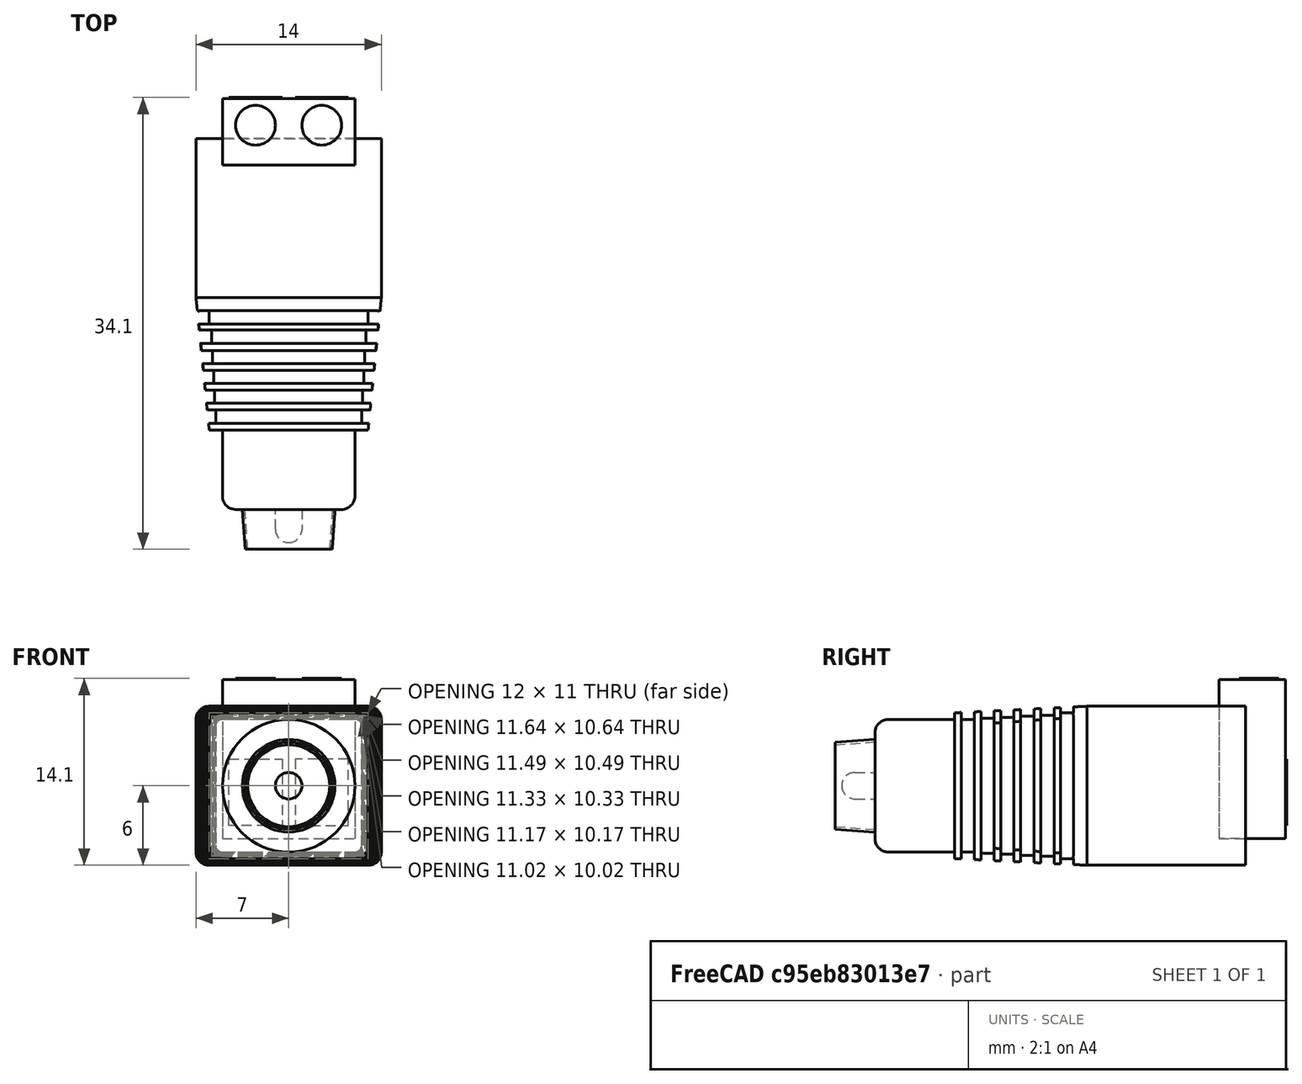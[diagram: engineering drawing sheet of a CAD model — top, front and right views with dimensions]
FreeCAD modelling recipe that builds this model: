
FCSTD DOCUMENT  (FreeCAD 1.1R20260414 (Git shallow))
Label: dc_to_2wire
License: All rights reserved
LicenseURL: https://en.wikipedia.org/wiki/All_rights_reserved
objects: Sketcher::SketchObject×9, PartDesign::Pad×7, App::Point×5, PartDesign::Plane×5, PartDesign::Body×4, App::Link×4, App::FeaturePython×4, PartDesign::Fillet×2, PartDesign::Mirrored×2, PartDesign::AdditiveLoft×1, PartDesign::SubtractivePipe×1, Assembly::JointGroup×1, Assembly::AssemblyObject×1
note: 64 computed .brp shape members not serialized (recipe doc carries the construction recipe); baked Part::Feature solids carry a one-line shape summary decoded from their .brp

FEATURE [App::Point] Origin001
  Role = Origin
FEATURE [Sketcher::SketchObject] Sketch
  ArcFitTolerance = 1e-06
  AttachmentSupport = -> [Origin]
  ExternalTypes = [0]
  FullyConstrained = true
  MakeInternals = false
  MapMode = 5
  Placement = pos=(0,0,0) rot=(1,0,0;1.5708rad)
  _ExternalGeoVersion = 1
  sketch-geometry (10):
    g0: LineSegment StartX=-6 StartY=-6 StartZ=0 EndX=6 EndY=-6 EndZ=0
    g1: LineSegment StartX=7 StartY=-5 StartZ=0 EndX=7 EndY=5 EndZ=0
    g2: LineSegment StartX=6 StartY=6 StartZ=0 EndX=-6 EndY=6 EndZ=0
    g3: LineSegment StartX=-7 StartY=5 StartZ=0 EndX=-7 EndY=-5 EndZ=0
    g4: ArcOfCircle CenterX=-6 CenterY=-5 CenterZ=0 NormalX=0 NormalY=0 NormalZ=1 AngleXU=0 Radius=1 StartAngle=3.14159 EndAngle=4.71239
    g5: ArcOfCircle CenterX=6 CenterY=-5 CenterZ=0 NormalX=0 NormalY=0 NormalZ=1 AngleXU=0 Radius=1 StartAngle=4.71239 EndAngle=6.28319
    g6: ArcOfCircle CenterX=6 CenterY=5 CenterZ=0 NormalX=0 NormalY=0 NormalZ=1 AngleXU=0 Radius=1 StartAngle=0 EndAngle=1.5708
    g7: ArcOfCircle CenterX=-6 CenterY=5 CenterZ=0 NormalX=0 NormalY=0 NormalZ=1 AngleXU=0 Radius=1 StartAngle=1.5708 EndAngle=3.14159
    g8: GeomPoint [constr] X=7 Y=6 Z=0
    g9: GeomPoint [constr] X=-2.33e-14 Y=2.6e-14 Z=0
  constraints (22):
    c: Tangent(g0,g4) = -1.5708
    c: Tangent(g0,g5) = -1.5708
    c: Tangent(g1,g5) = -1.5708
    c: Tangent(g1,g6) = -1.5708
    c: Tangent(g2,g6) = -1.5708
    c: Tangent(g2,g7) = -1.5708
    c: Tangent(g3,g7) = -1.5708
    c: Tangent(g3,g4) = -1.5708
    c: Horizontal(g0)
    c: Horizontal(g2)
    c: Vertical(g1)
    c: Vertical(g3)
    c: Equal(g4,g5)
    c: Equal(g5,g6)
    c: Equal(g6,g7)
    c: Symmetric(g2,g0,g9)
    c: PointOnObject(g8,g1)
    c: PointOnObject(g8,g2)
    c: Distance(g1,g3) = 14
    c: Distance(g0,g2) = 12
    c: Radius(g5) = 1
    c: Coincident(g9,g-1)
FEATURE [PartDesign::Pad] Pad
  Direction = (0,-1,2e-16)
  Length = 12
  Length2 = 10
  Profile = -> Sketch
  ReferenceAxis = -> Sketch [N_Axis]
  Refine = true
  SideType = 0
  Suppressed = false
  Type = 0
  Type2 = 0
FEATURE [PartDesign::Plane] DatumPlane
  AttachmentOffset = pos=(0,0,10) rot=(0,0,1;0rad)
  AttachmentSupport = -> [Pad]
  Length = 60
  MapMode = 5
  Placement = pos=(0,-22,2.2e-15) rot=(1,0,0;1.5708rad)
  ResizeMode = 0
  Width = 60
FEATURE [Sketcher::SketchObject] Sketch001
  ArcFitTolerance = 1e-06
  AttachmentSupport = -> [DatumPlane]
  ExternalTypes = [0]
  FullyConstrained = true
  MakeInternals = false
  MapMode = 5
  Placement = pos=(0,-22,2.2e-15) rot=(1,0,0;1.5708rad)
  _ExternalGeoVersion = 1
  sketch-geometry (10):
    g0: LineSegment StartX=-5 StartY=-5.5 StartZ=0 EndX=5 EndY=-5.5 EndZ=0
    g1: LineSegment StartX=6 StartY=-4.5 StartZ=0 EndX=6 EndY=4.5 EndZ=0
    g2: LineSegment StartX=5 StartY=5.5 StartZ=0 EndX=-5 EndY=5.5 EndZ=0
    g3: LineSegment StartX=-6 StartY=4.5 StartZ=0 EndX=-6 EndY=-4.5 EndZ=0
    g4: ArcOfCircle CenterX=-5 CenterY=-4.5 CenterZ=0 NormalX=0 NormalY=0 NormalZ=1 AngleXU=0 Radius=1 StartAngle=3.14159 EndAngle=4.71239
    g5: ArcOfCircle CenterX=5 CenterY=-4.5 CenterZ=0 NormalX=0 NormalY=0 NormalZ=1 AngleXU=0 Radius=1 StartAngle=4.71239 EndAngle=6.28319
    g6: ArcOfCircle CenterX=5 CenterY=4.5 CenterZ=0 NormalX=0 NormalY=0 NormalZ=1 AngleXU=0 Radius=1 StartAngle=0 EndAngle=1.5708
    g7: ArcOfCircle CenterX=-5 CenterY=4.5 CenterZ=0 NormalX=0 NormalY=0 NormalZ=1 AngleXU=0 Radius=1 StartAngle=1.5708 EndAngle=3.14159
    g8: GeomPoint [constr] X=6 Y=5.5 Z=0
    g9: GeomPoint [constr] X=0 Y=1.17e-14 Z=0
  constraints (22):
    c: Tangent(g0,g4) = -1.5708
    c: Tangent(g0,g5) = -1.5708
    c: Tangent(g1,g5) = -1.5708
    c: Tangent(g1,g6) = -1.5708
    c: Tangent(g2,g6) = -1.5708
    c: Tangent(g2,g7) = -1.5708
    c: Tangent(g3,g7) = -1.5708
    c: Tangent(g3,g4) = -1.5708
    c: Horizontal(g0)
    c: Horizontal(g2)
    c: Vertical(g1)
    c: Vertical(g3)
    c: Equal(g4,g5)
    c: Equal(g5,g6)
    c: Equal(g6,g7)
    c: Symmetric(g2,g0,g9)
    c: PointOnObject(g8,g1)
    c: PointOnObject(g8,g2)
    c: Distance(g1,g3) = 12
    c: Distance(g0,g2) = 11
    c: Radius(g5) = 1
    c: Coincident(g9,g-1)
FEATURE [PartDesign::AdditiveLoft] AdditiveLoft
  BaseFeature = -> Pad
  Closed = false
  Profile = -> Pad [Face10]
  Refine = true
  Ruled = false
  Sections = -> [Sketch001]
  Suppressed = false
FEATURE [Sketcher::SketchObject] Sketch002
  ArcFitTolerance = 1e-06
  AttachmentSupport = -> [AdditiveLoft]
  ExternalTypes = [0]
  FullyConstrained = true
  MakeInternals = false
  MapMode = 5
  Placement = pos=(0,-22,0) rot=(1,0,0;1.5708rad)
  _ExternalGeoVersion = 1
  sketch-geometry (1):
    g0: Circle CenterX=0 CenterY=0 CenterZ=0 NormalX=0 NormalY=0 NormalZ=1 AngleXU=0 Radius=5
  constraints (2):
    c: Diameter(g0) = 10
    c: Coincident(g0,g-1)
FEATURE [PartDesign::Pad] Pad001
  BaseFeature = -> AdditiveLoft
  Direction = (0,-1,2e-16)
  Length = 6
  Length2 = 10
  Profile = -> Sketch002
  ReferenceAxis = -> Sketch002 [N_Axis]
  Refine = true
  SideType = 0
  Suppressed = false
  Type = 0
  Type2 = 0
FEATURE [PartDesign::Fillet] Fillet
  Base = -> Pad001 [Edge55]
  BaseFeature = -> Pad001
  Radius = 1
  Refine = true
  SupportTransform = false
  Suppressed = false
  UseAllEdges = false
FEATURE [Sketcher::SketchObject] Sketch003
  ArcFitTolerance = 1e-06
  AttachmentSupport = -> [Origin]
  ExternalGeometry = -> [Fillet]
  ExternalTypes = [0]
  FullyConstrained = false
  MakeInternals = false
  MapMode = 5
  Placement = pos=(0,0,0) rot=(0.57735,0.57735,0.57735;2.0944rad)
  _ExternalGeoVersion = 1
  sketch-geometry (24):
    g0: LineSegment StartX=-13 StartY=6.5 StartZ=0 EndX=-14 EndY=6.5 EndZ=0
    g1: LineSegment StartX=-14 StartY=6.5 StartZ=0 EndX=-14 EndY=5.5 EndZ=0
    g2: LineSegment StartX=-14 StartY=5.5 StartZ=0 EndX=-13 EndY=5.5 EndZ=0
    g3: LineSegment StartX=-13 StartY=5.5 StartZ=0 EndX=-13 EndY=6.5 EndZ=0
    g4: LineSegment StartX=-14.4641 StartY=6.45747 StartZ=0 EndX=-15.4641 EndY=6.45747 EndZ=0
    g5: LineSegment StartX=-15.4641 StartY=6.45747 StartZ=0 EndX=-15.4641 EndY=5.3215 EndZ=0
    g6: LineSegment StartX=-15.4641 StartY=5.3215 StartZ=0 EndX=-14.4641 EndY=5.3215 EndZ=0
    g7: LineSegment StartX=-14.4641 StartY=5.3215 StartZ=0 EndX=-14.4641 EndY=6.45747 EndZ=0
    g8: LineSegment StartX=-15.9959 StartY=6.24299 StartZ=0 EndX=-16.9959 EndY=6.24299 EndZ=0
    g9: LineSegment StartX=-16.9959 StartY=6.24299 StartZ=0 EndX=-16.9959 EndY=5.24299 EndZ=0
    g10: LineSegment StartX=-16.9959 StartY=5.24299 StartZ=0 EndX=-15.9959 EndY=5.24299 EndZ=0
    g11: LineSegment StartX=-15.9959 StartY=5.24299 StartZ=0 EndX=-15.9959 EndY=6.24299 EndZ=0
    g12: LineSegment StartX=-17.4938 StartY=6.16449 StartZ=0 EndX=-18.4938 EndY=6.16449 EndZ=0
    g13: LineSegment StartX=-18.4938 StartY=6.16449 StartZ=0 EndX=-18.4938 EndY=5.16449 EndZ=0
    g14: LineSegment StartX=-18.4938 StartY=5.16449 StartZ=0 EndX=-17.4938 EndY=5.16449 EndZ=0
    g15: LineSegment StartX=-17.4938 StartY=5.16449 StartZ=0 EndX=-17.4938 EndY=6.16449 EndZ=0
    g16: LineSegment StartX=-18.9918 StartY=6.08598 StartZ=0 EndX=-19.9918 EndY=6.08598 EndZ=0
    g17: LineSegment StartX=-19.9918 StartY=6.08598 StartZ=0 EndX=-19.9918 EndY=5.08598 EndZ=0
    g18: LineSegment StartX=-19.9918 StartY=5.08598 StartZ=0 EndX=-18.9918 EndY=5.08598 EndZ=0
    g19: LineSegment StartX=-18.9918 StartY=5.08598 StartZ=0 EndX=-18.9918 EndY=6.08598 EndZ=0
    g20: LineSegment StartX=-20.4897 StartY=6.00748 StartZ=0 EndX=-21.4897 EndY=6.00748 EndZ=0
    g21: LineSegment StartX=-21.4897 StartY=6.00748 StartZ=0 EndX=-21.4897 EndY=5.00748 EndZ=0
    g22: LineSegment StartX=-21.4897 StartY=5.00748 StartZ=0 EndX=-20.4897 EndY=5.00748 EndZ=0
    g23: LineSegment StartX=-20.4897 StartY=5.00748 StartZ=0 EndX=-20.4897 EndY=6.00748 EndZ=0
  constraints (52):
    c: Coincident(g0,g1)
    c: Coincident(g1,g2)
    c: Coincident(g2,g3)
    c: Coincident(g3,g0)
    c: Horizontal(g0)
    c: Horizontal(g2)
    c: Vertical(g1)
    c: Vertical(g3)
    c: Distance(g1,g3) = 1
    c: Distance(g0,g2) = 1
    c: Distance(g-3,g3) = 1
    c: DistanceY(g-3,g0) = 0.5
    c: Coincident(g4,g5)
    c: Coincident(g8,g9)
    c: Coincident(g12,g13)
    c: Coincident(g16,g17)
    c: Coincident(g20,g21)
    c: Coincident(g5,g6)
    c: Coincident(g9,g10)
    c: Coincident(g13,g14)
    c: Coincident(g17,g18)
    c: Coincident(g21,g22)
    c: Coincident(g6,g7)
    c: Coincident(g10,g11)
    c: Coincident(g14,g15)
    c: Coincident(g18,g19)
    c: Coincident(g22,g23)
    c: Coincident(g7,g4)
    c: Coincident(g11,g8)
    c: Coincident(g15,g12)
    c: Coincident(g19,g16)
    c: Coincident(g23,g20)
    c: Horizontal(g4)
    c: Horizontal(g8)
    c: Horizontal(g12)
    c: Horizontal(g16)
    c: Horizontal(g20)
    c: Horizontal(g6)
    c: Horizontal(g10)
    c: Horizontal(g14)
    c: Horizontal(g18)
    c: Horizontal(g22)
    c: Vertical(g5)
    c: Vertical(g9)
    c: Vertical(g13)
    c: Vertical(g17)
    c: Vertical(g21)
    c: Vertical(g7)
    c: Vertical(g11)
    c: Vertical(g15)
    c: Vertical(g19)
    c: Vertical(g23)
FEATURE [PartDesign::SubtractivePipe] SubtractivePipe
  AuxiliaryCurvilinear = true
  AuxiliarySpineTangent = false
  BaseFeature = -> Fillet
  Binormal = (0,0,0)
  Mode = 0
  Profile = -> Sketch003
  Refine = true
  Spine = -> Fillet [Edge17,Edge16,Edge14,Edge12,Edge10,Edge8,Edge6,Edge7,Edge9,Edge11,Edge13,Edge15]
  SpineTangent = false
  Suppressed = false
  Transformation = 0
  Transition = 0
FEATURE [PartDesign::Body] Body  label="base"
  AllowCompound = true
  Group = -> [Sketch,Pad,DatumPlane,Sketch001,AdditiveLoft,Sketch002,Pad001,Fillet,Sketch003,SubtractivePipe]
  Origin = -> Origin
  Tip = -> SubtractivePipe
FEATURE [App::Point] Origin005  label="Origin006"
  Role = Origin
FEATURE [PartDesign::Plane] DatumPlane001
  Length = 60
  MapMode = 5
  Placement = pos=(0,1.3e-15,6) rot=(0,0,1;0rad)
  ResizeMode = 0
  Width = 60
FEATURE [Sketcher::SketchObject] Sketch006
  ArcFitTolerance = 1e-06
  AttachmentSupport = -> [DatumPlane001]
  ExternalTypes = [0]
  FullyConstrained = true
  MakeInternals = false
  MapMode = 5
  Placement = pos=(0,1.3e-15,6) rot=(0,0,1;0rad)
  _ExternalGeoVersion = 1
  sketch-geometry (5):
    g0: LineSegment StartX=-5 StartY=-2 StartZ=0 EndX=5 EndY=-2 EndZ=0
    g1: LineSegment StartX=5 StartY=-2 StartZ=0 EndX=5 EndY=3 EndZ=0
    g2: LineSegment StartX=5 StartY=3 StartZ=0 EndX=-5 EndY=3 EndZ=0
    g3: LineSegment StartX=-5 StartY=3 StartZ=0 EndX=-5 EndY=-2 EndZ=0
    g4: GeomPoint [constr] X=0 Y=0.5 Z=0
  constraints (13):
    c: Coincident(g0,g1)
    c: Coincident(g1,g2)
    c: Coincident(g2,g3)
    c: Coincident(g3,g0)
    c: Horizontal(g0)
    c: Horizontal(g2)
    c: Vertical(g1)
    c: Vertical(g3)
    c: Symmetric(g2,g0,g4)
    c: Distance(g1,g3) = 10
    c: Distance(g0,g2) = 5
    c: PointOnObject(g4,g-2)
    c: Distance(g-1,g0) = 2
FEATURE [PartDesign::Pad] Pad004
  Direction = (0,0,1)
  Length = 2
  Length2 = 10
  Placement = pos=(0,1.3e-15,6) rot=(0,0,1;0rad)
  Profile = -> Sketch006
  ReferenceAxis = -> Sketch006 [N_Axis]
  Refine = true
  SideType = 1
  Suppressed = false
  Type = 0
  Type2 = 0
FEATURE [PartDesign::Body] Body002  label="sockets"
  AllowCompound = true
  Group = -> [DatumPlane001,Sketch006,Pad004]
  Origin = -> Origin004
  Tip = -> Pad004
FEATURE [App::Point] Origin007  label="Origin009"
  Role = Origin
FEATURE [PartDesign::Plane] DatumPlane002
  AttachmentSupport = -> [Pad004]
  Length = 60
  MapMode = 5
  Placement = pos=(0,3,6) rot=(0,0.707107,0.707107;3.14159rad)
  ResizeMode = 0
  Width = 60
FEATURE [Sketcher::SketchObject] Sketch007
  ArcFitTolerance = 1e-06
  AttachmentSupport = -> [DatumPlane002]
  ExternalTypes = [0]
  FullyConstrained = true
  MakeInternals = false
  MapMode = 5
  Placement = pos=(0,3,6) rot=(0,0.707107,0.707107;3.14159rad)
  _ExternalGeoVersion = 1
  sketch-geometry (4):
    g0: LineSegment StartX=0.5 StartY=-4 StartZ=0 EndX=0.5 EndY=-9 EndZ=0
    g1: LineSegment StartX=0.5 StartY=-9 StartZ=0 EndX=4.5 EndY=-9 EndZ=0
    g2: LineSegment StartX=4.5 StartY=-9 StartZ=0 EndX=4.5 EndY=-4 EndZ=0
    g3: LineSegment StartX=4.5 StartY=-4 StartZ=0 EndX=0.5 EndY=-4 EndZ=0
  constraints (12):
    c: Coincident(g0,g1)
    c: Coincident(g1,g2)
    c: Coincident(g2,g3)
    c: Coincident(g3,g0)
    c: Vertical(g0)
    c: Vertical(g2)
    c: Horizontal(g1)
    c: Horizontal(g3)
    c: Distance(g0,g2) = 4
    c: Distance(g1,g3) = 5
    c: Distance(g-2,g0) = 0.5
    c: Distance(g-1,g3) = 4
FEATURE [PartDesign::Pad] Pad005
  Direction = (0,1,-2e-16)
  Length = 0.1
  Length2 = 10
  Placement = pos=(0,3,6) rot=(0,0.707107,0.707107;3.14159rad)
  Profile = -> Sketch007
  ReferenceAxis = -> Sketch007 [N_Axis]
  Refine = true
  SideType = 0
  Suppressed = false
  Type = 0
  Type2 = 0
FEATURE [PartDesign::Mirrored] Mirrored
  BaseFeature = -> Pad005
  MirrorPlane = -> Sketch007 [V_Axis]
  Originals = -> [Pad005]
  Placement = pos=(0,3,6) rot=(0,0.707107,0.707107;3.14159rad)
  Refine = true
  Suppressed = false
  TransformMode = 0
FEATURE [PartDesign::Plane] DatumPlane003
  AttachmentSupport = -> [Pad004]
  Length = 60
  MapMode = 5
  Placement = pos=(0,1.3e-15,8) rot=(0,0,1;0rad)
  ResizeMode = 0
  Width = 60
FEATURE [Sketcher::SketchObject] Sketch008
  ArcFitTolerance = 1e-06
  AttachmentSupport = -> [DatumPlane003]
  ExternalTypes = [0]
  FullyConstrained = true
  MakeInternals = false
  MapMode = 5
  Placement = pos=(0,1.3e-15,8) rot=(0,0,1;0rad)
  _ExternalGeoVersion = 1
  sketch-geometry (1):
    g0: Circle CenterX=-2.5 CenterY=1 CenterZ=0 NormalX=0 NormalY=0 NormalZ=1 AngleXU=0 Radius=1.5
  constraints (3):
    c: Diameter(g0) = 3
    c: Distance(g0,g-2) = 1
    c: Distance(g0,g-1) = 1
FEATURE [PartDesign::Pad] Pad006
  BaseFeature = -> Mirrored
  Direction = (0,0,1)
  Length = 0.1
  Length2 = 10
  Placement = pos=(0,3,6) rot=(0,0.707107,0.707107;3.14159rad)
  Profile = -> Sketch008
  ReferenceAxis = -> Sketch008 [N_Axis]
  Refine = true
  SideType = 0
  Suppressed = false
  Type = 0
  Type2 = 0
FEATURE [PartDesign::Mirrored] Mirrored001
  BaseFeature = -> Pad006
  MirrorPlane = -> Sketch008 [V_Axis]
  Originals = -> [Pad006]
  Placement = pos=(0,3,6) rot=(0,0.707107,0.707107;3.14159rad)
  Refine = true
  Suppressed = false
  TransformMode = 0
FEATURE [PartDesign::Body] Body003  label="connectors"
  AllowCompound = true
  Group = -> [DatumPlane002,Sketch007,Pad005,Mirrored,DatumPlane003,Sketch008,Pad006,Mirrored001]
  Origin = -> Origin006
  Tip = -> Mirrored001
FEATURE [App::Point] Origin009  label="Origin011"
  Role = Origin
FEATURE [PartDesign::Plane] DatumPlane004
  AttachmentSupport = -> [SubtractivePipe]
  Length = 60
  MapMode = 5
  Placement = pos=(0,-28,0) rot=(1,0,0;1.5708rad)
  ResizeMode = 0
  Width = 60
FEATURE [Sketcher::SketchObject] Sketch009
  ArcFitTolerance = 1e-06
  AttachmentSupport = -> [DatumPlane004]
  ExternalTypes = [0]
  FullyConstrained = true
  MakeInternals = false
  MapMode = 5
  Placement = pos=(0,-28,0) rot=(1,0,0;1.5708rad)
  _ExternalGeoVersion = 1
  sketch-geometry (2):
    g0: Circle CenterX=0 CenterY=0 CenterZ=0 NormalX=0 NormalY=0 NormalZ=1 AngleXU=0 Radius=3.5
    g1: Circle CenterX=0 CenterY=0 CenterZ=0 NormalX=0 NormalY=0 NormalZ=1 AngleXU=0 Radius=3.3
  constraints (4):
    c: Diameter(g0) = 7
    c: Coincident(g0,g-1)
    c: Coincident(g1,g0)
    c: Distance(g1,g0) = 0.2
FEATURE [PartDesign::Pad] Pad007
  Direction = (0,-1,2e-16)
  Length = 3
  Length2 = 10
  Placement = pos=(0,-28,0) rot=(1,0,0;1.5708rad)
  Profile = -> Sketch009
  ReferenceAxis = -> Sketch009 [N_Axis]
  Refine = true
  SideType = 0
  Suppressed = false
  TaperAngle = -4
  Type = 0
  Type2 = 0
FEATURE [Sketcher::SketchObject] Sketch010
  ArcFitTolerance = 1e-06
  AttachmentSupport = -> [DatumPlane004]
  ExternalTypes = [0]
  FullyConstrained = true
  MakeInternals = false
  MapMode = 5
  Placement = pos=(0,-28,0) rot=(1,0,0;1.5708rad)
  _ExternalGeoVersion = 1
  sketch-geometry (1):
    g0: Circle CenterX=0 CenterY=0 CenterZ=0 NormalX=0 NormalY=0 NormalZ=1 AngleXU=0 Radius=1
  constraints (2):
    c: Diameter(g0) = 2
    c: Coincident(g0,g-1)
FEATURE [PartDesign::Pad] Pad008
  BaseFeature = -> Pad007
  Direction = (0,-1,2e-16)
  Length = 2.5
  Length2 = 10
  Placement = pos=(0,-28,0) rot=(1,0,0;1.5708rad)
  Profile = -> Sketch010
  ReferenceAxis = -> Sketch010 [N_Axis]
  Refine = true
  SideType = 0
  Suppressed = false
  Type = 0
  Type2 = 0
FEATURE [PartDesign::Fillet] Fillet001
  Base = -> Pad008 [Edge9]
  BaseFeature = -> Pad008
  Placement = pos=(0,-28,0) rot=(1,0,0;1.5708rad)
  Radius = 1
  Refine = true
  SupportTransform = false
  Suppressed = false
  UseAllEdges = false
FEATURE [PartDesign::Body] Body004  label="aux"
  AllowCompound = true
  Group = -> [DatumPlane004,Sketch009,Pad007,Sketch010,Pad008,Fillet001]
  Origin = -> Origin008
  Tip = -> Fillet001
FEATURE [App::Point] Origin011  label="Origin014"
  Role = Origin
FEATURE [App::Link] base  label="base001"
  LinkedObject = -> Body
FEATURE [App::FeaturePython] GroundedJoint  # Assembly grounded joint (typed FeaturePython)
  ObjectToGround = -> base
FEATURE [App::Link] connectors  label="connectors001"
  LinkPlacement = pos=(1,1,1) rot=(0,0,1;0rad)
  LinkedObject = -> Body003
  Placement = pos=(1,1,1) rot=(0,0,1;0rad)
FEATURE [App::Link] sockets  label="sockets001"
  LinkPlacement = pos=(1,1,1) rot=(0,0,1;0rad)
  LinkedObject = -> Body002
  Placement = pos=(1,1,1) rot=(0,0,1;0rad)
FEATURE [App::Link] aux  label="aux001"
  LinkPlacement = pos=(4e-16,-3.6e-15,-1.1e-15) rot=(0,0,1;0rad)
  LinkedObject = -> Body004
  Placement = pos=(4e-16,-3.6e-15,-1.1e-15) rot=(0,0,1;0rad)
FEATURE [App::FeaturePython] Joint  label="Fixed"  # Assembly joint (typed FeaturePython)
  Angle = 0
  AngleMax = 0
  AngleMin = 0
  Detach1 = false
  Detach2 = false
  Distance = 0
  Distance2 = 0
  EnableAngleMax = false
  EnableAngleMin = false
  EnableLengthMax = false
  EnableLengthMin = false
  JointType = 0 (Fixed)
  LengthMax = 0
  LengthMin = 0
  Placement1 = pos=(0,-28,1e-15) rot=(0.57735,0.57735,0.57735;4.18879rad)
  Placement2 = pos=(4e-16,-28,-1e-16) rot=(0.57735,0.57735,0.57735;4.18879rad)
  Reference1 = -> aux [Face3,Edge1]
  Reference2 = -> base [Face95,Face95]
  Suppressed = false
FEATURE [App::FeaturePython] Joint001  label="Fixed008"  # Assembly joint (typed FeaturePython)
  Angle = 0
  AngleMax = 0
  AngleMin = 0
  Detach1 = false
  Detach2 = false
  Distance = 0
  Distance2 = 0
  EnableAngleMax = false
  EnableAngleMin = false
  EnableLengthMax = false
  EnableLengthMin = false
  JointType = 0 (Fixed)
  LengthMax = 0
  LengthMin = 0
  Offset1 = pos=(0,0.5,0) rot=(0,0,1;0rad)
  Offset2 = pos=(0,0,0) rot=(0,0,1;1.5708rad)
  Placement1 = pos=(-9e-16,3,2) rot=(0.57735,-0.57735,0.57735;2.0944rad)
  Placement2 = pos=(0,3,2) rot=(0.57735,0.57735,0.57735;4.18879rad)
  Reference1 = -> connectors [Face11,Vertex9]
  Reference2 = -> sockets [Face3,Face3]
  Suppressed = false
FEATURE [App::FeaturePython] Joint002  label="Fixed010"  # Assembly joint (typed FeaturePython)
  Angle = 0
  AngleMax = 0
  AngleMin = 0
  Detach1 = false
  Detach2 = false
  Distance = 0
  Distance2 = 0
  EnableAngleMax = false
  EnableAngleMin = false
  EnableLengthMax = false
  EnableLengthMin = false
  JointType = 0 (Fixed)
  LengthMax = 0
  LengthMin = 0
  Offset2 = pos=(3,1,-1) rot=(0,0,1;1.5708rad)
  Placement1 = pos=(1e-16,-2,2) rot=(1,0,0;1.5708rad)
  Placement2 = pos=(1,-1,3) rot=(1,0,0;4.71239rad)
  Reference1 = -> sockets [Face1,Face1]
  Reference2 = -> base [Face25,Face25]
  Suppressed = false
FEATURE [Assembly::JointGroup] Joints
  Group = -> [GroundedJoint,Joint,Joint001,Joint002]
FEATURE [Assembly::AssemblyObject] Assembly
  Group = -> [Joints,base,GroundedJoint,connectors,sockets,aux,Joint,Joint001,Joint002]
  Origin = -> Origin010
  Type = Assembly
